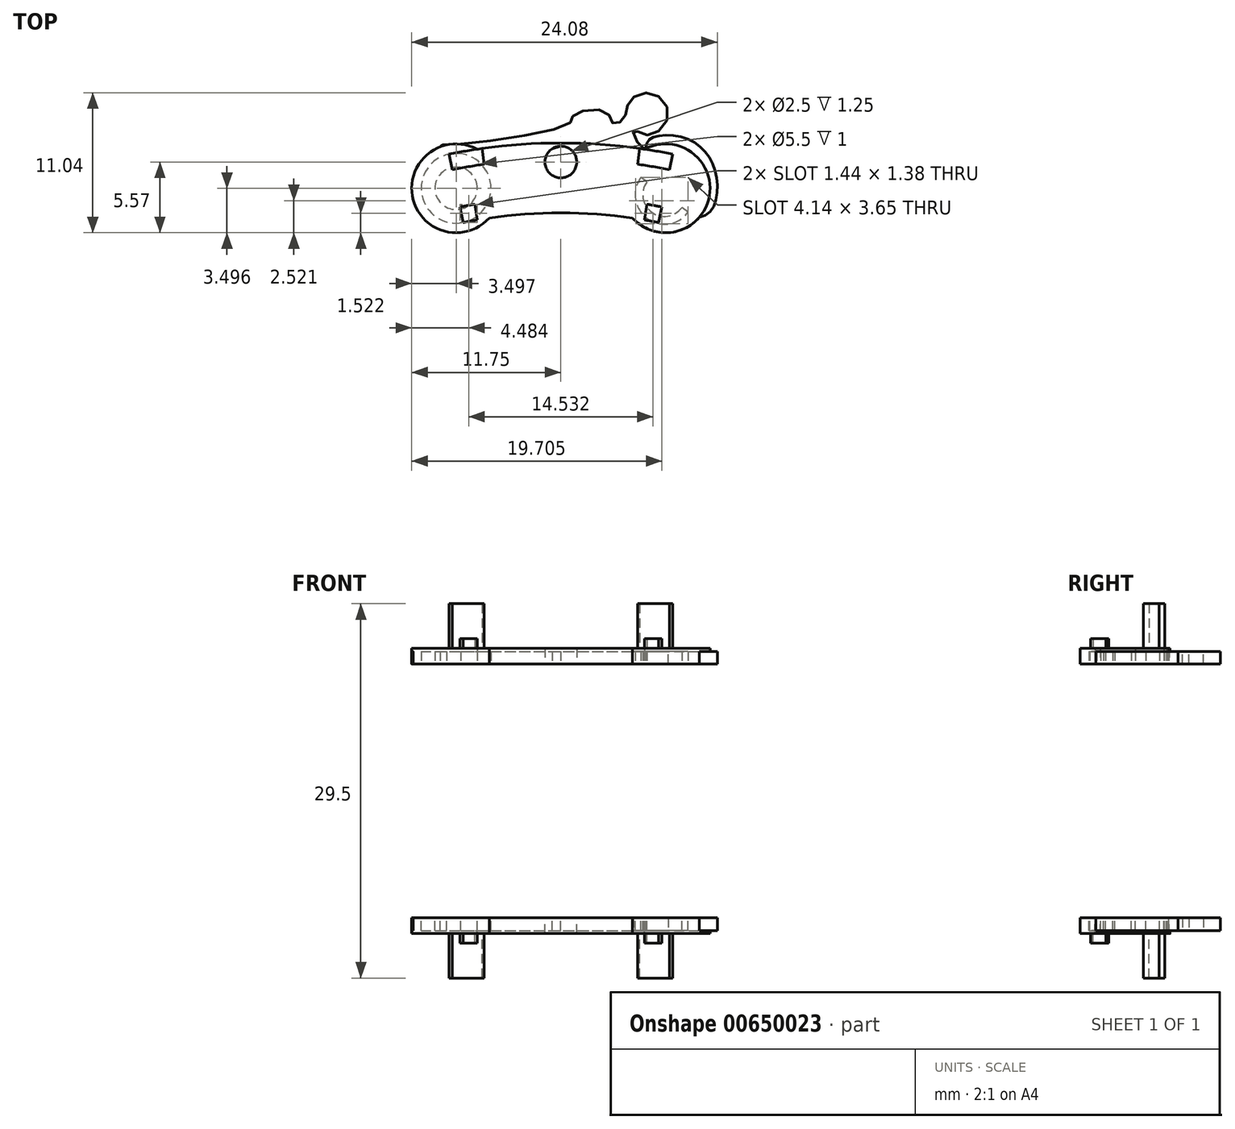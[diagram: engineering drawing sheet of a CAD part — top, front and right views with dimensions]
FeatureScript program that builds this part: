
annotation { "Feature Type Name" : "Feature", "Feature Type Description" : "" }
export const myFeature = defineFeature(function(context is Context, id is Id, definition is map)
    precondition{}
    {
        {
            var Q0;
            Q0=qCreatedBy(makeId("Top.planeOp"),FACE);
            var sketch = newSketch(context, id + "F0", { "sketchPlane" : qUnion([Q0])});
            skCircle(sketch, "E0", {"center": v(0, 0) * mm, "radius": 39 * mm});
            skCircle(sketch, "E1", {"center": v(0, 0) * mm, "radius": 44.5 * mm});
            skCircle(sketch, "E2", {"center": v(0, 43) * mm, "radius": 1.25 * mm});
            skCircle(sketch, "E3", {"center": v(0, 43) * mm, "radius": 6 * mm});
            skLineSegment(sketch, "E4", {"start": v(-7.7, 38.23) * mm, "end": v(-8.8, 43.62) * mm});
            skLineSegment(sketch, "E5", {"start": v(7.7, 38.23) * mm, "end": v(8.8, 43.62) * mm});
            skLineSegment(sketch, "E6", {"start": v(-7.5, 43.86) * mm, "end": v(-6.58, 38.44) * mm});
            skLineSegment(sketch, "E7", {"start": v(6.58, 38.44) * mm, "end": v(7.5, 43.86) * mm});
            skCircle(sketch, "E8", {"center": v(0, 0) * mm, "radius": 40.25 * mm});
            skCircle(sketch, "E9", {"center": v(0, 0) * mm, "radius": 43.25 * mm});
            skSolve(sketch);
        }
        {
            var Q0;
            {var subQ0=sQuery(id+"F0.wireOp",EDGE,"E7");var subQ1=sQuery(id+"F0.wireOp",EDGE,"E1");var subQ2=makeQuery(id+"F0.imprint","INTERSECT",VERTEX,{"derivedFrom":[subQ1,subQ0]});Q0=makeQuery(id+"F0.imprint","IMPRINT",FACE,{"disambiguationData":[TD([[makeQuery(id+"F0.imprint","IMPRINT",EDGE,{"disambiguationData":[TD([[subQ2,-1.0]])],"derivedFrom":subQ1}),1.0]])]});}
            var Q1;
            {var subQ0=sQuery(id+"F0.wireOp",EDGE,"E6");var subQ1=sQuery(id+"F0.wireOp",EDGE,"E1");var subQ2=makeQuery(id+"F0.imprint","INTERSECT",VERTEX,{"derivedFrom":[subQ1,subQ0]});Q1=makeQuery(id+"F0.imprint","IMPRINT",FACE,{"disambiguationData":[TD([[makeQuery(id+"F0.imprint","IMPRINT",EDGE,{"disambiguationData":[TD([[subQ2,1.0]])],"derivedFrom":subQ1}),1.0]])]});}
            var Q2;
            {var subQ0=sQuery(id+"F0.wireOp",EDGE,"E3");var subQ1=sQuery(id+"F0.wireOp",EDGE,"E1");var subQ2=makeQuery(id+"F0.imprint","INTERSECT",VERTEX,{"disambiguationData":[OD(0.0)],"derivedFrom":[subQ1,subQ0]});Q2=makeQuery(id+"F0.imprint","IMPRINT",FACE,{"disambiguationData":[TD([[makeQuery(id+"F0.imprint","IMPRINT",EDGE,{"disambiguationData":[TD([[subQ2,-1.0]])],"derivedFrom":subQ1}),1.0]])]});}
            var Q3;
            {var subQ0=sQuery(id+"F0.wireOp",EDGE,"E8");var subQ1=sQuery(id+"F0.wireOp",EDGE,"E3");var subQ2=makeQuery(id+"F0.imprint","INTERSECT",VERTEX,{"disambiguationData":[OD(1.0)],"derivedFrom":[subQ1,subQ0]});Q3=makeQuery(id+"F0.imprint","IMPRINT",FACE,{"disambiguationData":[TD([[makeQuery(id+"F0.imprint","IMPRINT",EDGE,{"disambiguationData":[TD([[subQ2,-1.0]])],"derivedFrom":subQ1}),-1.0]])]});}
            var Q4;
            {var subQ3=sQuery(id+"F0.wireOp",EDGE,"E9");var subQ5=sQuery(id+"F0.wireOp",EDGE,"E2");var subQ6=makeQuery(id+"F0.imprint","INTERSECT",VERTEX,{"disambiguationData":[OD(0.0)],"derivedFrom":[subQ5,subQ3]});Q4=makeQuery(id+"F0.imprint","IMPRINT",FACE,{"disambiguationData":[TD([[makeQuery(id+"F0.imprint","IMPRINT",EDGE,{"disambiguationData":[TD([[subQ6,1.0]])],"derivedFrom":subQ5}),-1.0]])]});}
            var Q5;
            {var subQ0=sQuery(id+"F0.wireOp",EDGE,"E9");var subQ1=sQuery(id+"F0.wireOp",EDGE,"E3");var subQ2=makeQuery(id+"F0.imprint","INTERSECT",VERTEX,{"disambiguationData":[OD(0.0)],"derivedFrom":[subQ1,subQ0]});Q5=makeQuery(id+"F0.imprint","IMPRINT",FACE,{"disambiguationData":[TD([[makeQuery(id+"F0.imprint","IMPRINT",EDGE,{"disambiguationData":[TD([[subQ2,-1.0]])],"derivedFrom":subQ1}),-1.0]])]});}
            var Q6;
            {var subQ0=sQuery(id+"F0.wireOp",EDGE,"E6");var subQ1=sQuery(id+"F0.wireOp",EDGE,"E0");var subQ2=makeQuery(id+"F0.imprint","INTERSECT",VERTEX,{"derivedFrom":[subQ1,subQ0]});Q6=makeQuery(id+"F0.imprint","IMPRINT",FACE,{"disambiguationData":[TD([[makeQuery(id+"F0.imprint","IMPRINT",EDGE,{"disambiguationData":[TD([[subQ2,1.0]])],"derivedFrom":subQ1}),-1.0]])]});}
            var Q7;
            {var subQ0=sQuery(id+"F0.wireOp",EDGE,"E3");var subQ1=sQuery(id+"F0.wireOp",EDGE,"E0");var subQ2=makeQuery(id+"F0.imprint","INTERSECT",VERTEX,{"disambiguationData":[OD(0.0)],"derivedFrom":[subQ1,subQ0]});Q7=makeQuery(id+"F0.imprint","IMPRINT",FACE,{"disambiguationData":[TD([[makeQuery(id+"F0.imprint","IMPRINT",EDGE,{"disambiguationData":[TD([[subQ2,-1.0]])],"derivedFrom":subQ1}),-1.0]])]});}
            var Q8;
            {var subQ0=sQuery(id+"F0.wireOp",EDGE,"E7");var subQ1=sQuery(id+"F0.wireOp",EDGE,"E0");var subQ2=makeQuery(id+"F0.imprint","INTERSECT",VERTEX,{"derivedFrom":[subQ1,subQ0]});Q8=makeQuery(id+"F0.imprint","IMPRINT",FACE,{"disambiguationData":[TD([[makeQuery(id+"F0.imprint","IMPRINT",EDGE,{"disambiguationData":[TD([[subQ2,-1.0]])],"derivedFrom":subQ1}),-1.0]])]});}
            var Q9;
            {var subQ0=sQuery(id+"F0.wireOp",EDGE,"E8");var subQ1=sQuery(id+"F0.wireOp",EDGE,"E5");var subQ2=makeQuery(id+"F0.imprint","INTERSECT",VERTEX,{"derivedFrom":[subQ1,subQ0]});Q9=makeQuery(id+"F0.imprint","IMPRINT",FACE,{"disambiguationData":[TD([[makeQuery(id+"F0.imprint","IMPRINT",EDGE,{"disambiguationData":[TD([[subQ2,-1.0]])],"derivedFrom":subQ1}),1.0]])]});}
            var Q10;
            {var subQ0=sQuery(id+"F0.wireOp",EDGE,"E8");var subQ1=sQuery(id+"F0.wireOp",EDGE,"E4");var subQ2=makeQuery(id+"F0.imprint","INTERSECT",VERTEX,{"derivedFrom":[subQ1,subQ0]});Q10=makeQuery(id+"F0.imprint","IMPRINT",FACE,{"disambiguationData":[TD([[makeQuery(id+"F0.imprint","IMPRINT",EDGE,{"disambiguationData":[TD([[subQ2,-1.0]])],"derivedFrom":subQ1}),-1.0]])]});}
            extrude(context, id + "F1", {"entities" : qUnion([Q0, Q1, Q2, Q3, Q4, Q5, Q6, Q7, Q8, Q9, Q10]), "depth" : 1.25 * mm, "offsetDistance" : 25 * mm});
        }
        {
            var Q0;
            Q0=qCreatedBy(makeId("Top.planeOp"),FACE);
            var sketch = newSketch(context, id + "F2", { "sketchPlane" : qUnion([Q0])});
            skCircle(sketch, "E10", {"center": v(0, 0) * mm, "radius": 39 * mm});
            skCircle(sketch, "E11", {"center": v(0, 0) * mm, "radius": 44.5 * mm});
            skCircle(sketch, "E12", {"center": v(0, 43) * mm, "radius": 0.85 * mm});
            skCircle(sketch, "E13", {"center": v(0, 43) * mm, "radius": 6 * mm});
            skLineSegment(sketch, "E14", {"start": v(-7.7, 38.23) * mm, "end": v(-8.8, 43.62) * mm});
            skLineSegment(sketch, "E15", {"start": v(7.7, 38.23) * mm, "end": v(8.8, 43.62) * mm});
            skLineSegment(sketch, "E16", {"start": v(-6.2, 44.06) * mm, "end": v(-5.44, 38.62) * mm});
            skLineSegment(sketch, "E17", {"start": v(5.44, 38.62) * mm, "end": v(6.2, 44.06) * mm});
            skCircle(sketch, "E18", {"center": v(0, 0) * mm, "radius": 40.25 * mm});
            skCircle(sketch, "E19", {"center": v(0, 0) * mm, "radius": 43.25 * mm});
            skSolve(sketch);
        }
        {
            var Q0;
            {var subQ0=sQuery(id+"F2.wireOp",EDGE,"E15");var subQ1=sQuery(id+"F2.wireOp",EDGE,"E11");var subQ2=makeQuery(id+"F2.imprint","INTERSECT",VERTEX,{"derivedFrom":[subQ1,subQ0]});Q0=makeQuery(id+"F2.imprint","IMPRINT",FACE,{"disambiguationData":[TD([[makeQuery(id+"F2.imprint","IMPRINT",EDGE,{"disambiguationData":[TD([[subQ2,-1.0]])],"derivedFrom":subQ1}),1.0]])]});}
            var Q1;
            {var subQ0=sQuery(id+"F2.wireOp",EDGE,"E14");var subQ1=sQuery(id+"F2.wireOp",EDGE,"E11");var subQ2=makeQuery(id+"F2.imprint","INTERSECT",VERTEX,{"derivedFrom":[subQ1,subQ0]});Q1=makeQuery(id+"F2.imprint","IMPRINT",FACE,{"disambiguationData":[TD([[makeQuery(id+"F2.imprint","IMPRINT",EDGE,{"disambiguationData":[TD([[subQ2,1.0]])],"derivedFrom":subQ1}),1.0]])]});}
            extrude(context, id + "F3", {"entities" : qUnion([Q0, Q1]), "operationType" : NewBodyOperationType.ADD, "depth" : 4.75 * mm, "offsetDistance" : 25 * mm});
        }
        {
            var Q0;
            Q0=qCreatedBy(makeId("Top.planeOp"),FACE);
            var sketch = newSketch(context, id + "F4", { "sketchPlane" : qUnion([Q0])});
            skCircle(sketch, "E20", {"center": v(0, 0) * mm, "radius": 39 * mm});
            skCircle(sketch, "E21", {"center": v(0, 0) * mm, "radius": 44.5 * mm});
            skCircle(sketch, "E22", {"center": v(0, 43) * mm, "radius": 0.85 * mm});
            skCircle(sketch, "E23", {"center": v(0, 43) * mm, "radius": 6 * mm});
            skLineSegment(sketch, "E24", {"start": v(-7.7, 38.23) * mm, "end": v(-8.8, 43.62) * mm});
            skLineSegment(sketch, "E25", {"start": v(7.7, 38.23) * mm, "end": v(8.8, 43.62) * mm});
            skLineSegment(sketch, "E26", {"start": v(-7.5, 43.86) * mm, "end": v(-6.58, 38.44) * mm});
            skLineSegment(sketch, "E27", {"start": v(6.58, 38.44) * mm, "end": v(7.5, 43.86) * mm});
            skCircle(sketch, "E28", {"center": v(0, 0) * mm, "radius": 40.25 * mm});
            skCircle(sketch, "E29", {"center": v(0, 0) * mm, "radius": 43.25 * mm});
            skSolve(sketch);
        }
        {
            var Q0;
            {var subQ0=sQuery(id+"F4.wireOp",EDGE,"E24");var subQ1=sQuery(id+"F4.wireOp",EDGE,"E20");var subQ2=makeQuery(id+"F4.imprint","INTERSECT",VERTEX,{"derivedFrom":[subQ1,subQ0]});Q0=makeQuery(id+"F4.imprint","IMPRINT",FACE,{"disambiguationData":[TD([[makeQuery(id+"F4.imprint","IMPRINT",EDGE,{"disambiguationData":[TD([[subQ2,1.0]])],"derivedFrom":subQ1}),-1.0]])]});}
            var Q1;
            {var subQ0=sQuery(id+"F4.wireOp",EDGE,"E25");var subQ1=sQuery(id+"F4.wireOp",EDGE,"E20");var subQ2=makeQuery(id+"F4.imprint","INTERSECT",VERTEX,{"derivedFrom":[subQ1,subQ0]});Q1=makeQuery(id+"F4.imprint","IMPRINT",FACE,{"disambiguationData":[TD([[makeQuery(id+"F4.imprint","IMPRINT",EDGE,{"disambiguationData":[TD([[subQ2,-1.0]])],"derivedFrom":subQ1}),-1.0]])]});}
            extrude(context, id + "F5", {"entities" : qUnion([Q0, Q1]), "operationType" : NewBodyOperationType.ADD, "depth" : 2 * mm, "offsetDistance" : 25 * mm});
        }
        {
            var Q0;
            {var subQ0=sQuery(id+"F4.wireOp",EDGE,"E28");var subQ1=sQuery(id+"F4.wireOp",EDGE,"E20");var subQ2=sQuery(id+"F2.wireOp",EDGE,"E19");var subQ3=sQuery(id+"F2.wireOp",EDGE,"E11");Q0=makeQuery(id+"F5.boolean.opBoolean","MERGE",FACE,{"derivedFrom":[makeQuery(id+"F3.boolean.opBoolean","MERGE",FACE,{"derivedFrom":[makeQuery(id+"F1.opExtrude","CAP_FACE",FACE,{"disambiguationData":[OSD([sQuery(id+"F0.wireOp",EDGE,"E0"),sQuery(id+"F0.wireOp",EDGE,"E1"),sQuery(id+"F0.wireOp",EDGE,"E2"),sQuery(id+"F0.wireOp",EDGE,"E4"),sQuery(id+"F0.wireOp",EDGE,"E5"),sQuery(id+"F0.wireOp",EDGE,"E6"),sQuery(id+"F0.wireOp",EDGE,"E7"),sQuery(id+"F0.wireOp",EDGE,"E8"),sQuery(id+"F0.wireOp",EDGE,"E9")])],"isStart":true}),makeQuery(id+"F3.opExtrude","CAP_FACE",FACE,{"disambiguationData":[OSD([subQ3,sQuery(id+"F2.wireOp",EDGE,"E15"),sQuery(id+"F2.wireOp",EDGE,"E17"),subQ2])],"isStart":true}),makeQuery(id+"F3.opExtrude","CAP_FACE",FACE,{"disambiguationData":[OSD([subQ3,sQuery(id+"F2.wireOp",EDGE,"E14"),sQuery(id+"F2.wireOp",EDGE,"E16"),subQ2])],"isStart":true})]}),makeQuery(id+"F5.opExtrude","CAP_FACE",FACE,{"disambiguationData":[OSD([subQ1,sQuery(id+"F4.wireOp",EDGE,"E25"),sQuery(id+"F4.wireOp",EDGE,"E27"),subQ0])],"isStart":true}),makeQuery(id+"F5.opExtrude","CAP_FACE",FACE,{"disambiguationData":[OSD([subQ1,sQuery(id+"F4.wireOp",EDGE,"E24"),sQuery(id+"F4.wireOp",EDGE,"E26"),subQ0])],"isStart":true})]});}
            var sketch = newSketch(context, id + "F6", { "sketchPlane" : qUnion([Q0])});
            skCircle(sketch, "E30", {"center": v(-8.25, -40.93) * mm, "radius": 3.5 * mm});
            skCircle(sketch, "E31", {"center": v(8.25, -40.93) * mm, "radius": 3.5 * mm});
            skSolve(sketch);
        }
        {
            var Q0;
            Q0 = qSketchRegion(id + "F6", true);
            extrude(context, id + "F7", {"entities" : qUnion([Q0]), "operationType" : NewBodyOperationType.ADD, "oppositeDirection" : true, "depth" : 1.25 * mm, "offsetDistance" : 25 * mm});
        }
        {
            var Q0;
            {var subQ0=sQuery(id+"F4.wireOp",EDGE,"E28");var subQ1=sQuery(id+"F4.wireOp",EDGE,"E20");var subQ2=sQuery(id+"F2.wireOp",EDGE,"E19");var subQ3=sQuery(id+"F2.wireOp",EDGE,"E11");Q0=makeQuery(id+"F7.boolean.opBoolean","MERGE",FACE,{"derivedFrom":[makeQuery(id+"F5.boolean.opBoolean","MERGE",FACE,{"derivedFrom":[makeQuery(id+"F3.boolean.opBoolean","MERGE",FACE,{"derivedFrom":[makeQuery(id+"F1.opExtrude","CAP_FACE",FACE,{"disambiguationData":[OSD([sQuery(id+"F0.wireOp",EDGE,"E0"),sQuery(id+"F0.wireOp",EDGE,"E1"),sQuery(id+"F0.wireOp",EDGE,"E2"),sQuery(id+"F0.wireOp",EDGE,"E4"),sQuery(id+"F0.wireOp",EDGE,"E5"),sQuery(id+"F0.wireOp",EDGE,"E6"),sQuery(id+"F0.wireOp",EDGE,"E7"),sQuery(id+"F0.wireOp",EDGE,"E8"),sQuery(id+"F0.wireOp",EDGE,"E9")])],"isStart":true}),makeQuery(id+"F3.opExtrude","CAP_FACE",FACE,{"disambiguationData":[OSD([subQ3,sQuery(id+"F2.wireOp",EDGE,"E15"),sQuery(id+"F2.wireOp",EDGE,"E17"),subQ2])],"isStart":true}),makeQuery(id+"F3.opExtrude","CAP_FACE",FACE,{"disambiguationData":[OSD([subQ3,sQuery(id+"F2.wireOp",EDGE,"E14"),sQuery(id+"F2.wireOp",EDGE,"E16"),subQ2])],"isStart":true})]}),makeQuery(id+"F5.opExtrude","CAP_FACE",FACE,{"disambiguationData":[OSD([subQ1,sQuery(id+"F4.wireOp",EDGE,"E25"),sQuery(id+"F4.wireOp",EDGE,"E27"),subQ0])],"isStart":true}),makeQuery(id+"F5.opExtrude","CAP_FACE",FACE,{"disambiguationData":[OSD([subQ1,sQuery(id+"F4.wireOp",EDGE,"E24"),sQuery(id+"F4.wireOp",EDGE,"E26"),subQ0])],"isStart":true})]}),makeQuery(id+"F7.opExtrude","CAP_FACE",FACE,{"disambiguationData":[OSD([sQuery(id+"F6.wireOp",EDGE,"E30")])],"isStart":true}),makeQuery(id+"F7.opExtrude","CAP_FACE",FACE,{"disambiguationData":[OSD([sQuery(id+"F6.wireOp",EDGE,"E31")])],"isStart":true})]});}
            var sketch = newSketch(context, id + "F8", { "sketchPlane" : qUnion([Q0])});
            skPoint(sketch, "E32.19.internal.snap0", {"position": v(0, -39) * mm});
            skFitSpline(sketch, "E32", {"points": [v(-9.52, -44.2) * mm, v(-9.01, -44.34) * mm, v(0.7, -46.06) * mm, v(1, -46.68) * mm, v(3.57, -46.95) * mm, v(4.12, -46.04) * mm, v(4.97, -46.43) * mm, v(5.33, -47.68) * mm, v(7.05, -48.44) * mm, v(8.48, -46.78) * mm, v(7.01, -45.12) * mm, v(5.85, -45.47) * mm, v(5.7, -45.23) * mm, v(6.6, -44) * mm, v(6.86, -44.64) * mm, v(10.09, -44.77) * mm, v(12.3, -41.5) * mm, v(10.9, -38.63) * mm, v(2.21, -43.47) * mm, v(0, -44.25) * mm, v(-9.77, -40.16) * mm, v(-10.2, -40.1) * mm, v(-11.62, -39.98) * mm, v(-9.52, -44.2) * mm]});
            skSolve(sketch);
        }
        {
            var Q0;
            Q0 = qSketchRegion(id + "F8", true);
            extrude(context, id + "F9", {"entities" : qUnion([Q0]), "operationType" : NewBodyOperationType.ADD, "oppositeDirection" : true, "depth" : 1 * mm, "offsetDistance" : 25 * mm});
        }
        {
            var Q0;
            {var subQ0=sQuery(id+"F4.wireOp",EDGE,"E28");var subQ1=sQuery(id+"F4.wireOp",EDGE,"E20");var subQ2=sQuery(id+"F2.wireOp",EDGE,"E19");var subQ3=sQuery(id+"F2.wireOp",EDGE,"E11");Q0=makeQuery(id+"F9.boolean.opBoolean","MERGE",FACE,{"derivedFrom":[makeQuery(id+"F7.boolean.opBoolean","MERGE",FACE,{"derivedFrom":[makeQuery(id+"F5.boolean.opBoolean","MERGE",FACE,{"derivedFrom":[makeQuery(id+"F3.boolean.opBoolean","MERGE",FACE,{"derivedFrom":[makeQuery(id+"F1.opExtrude","CAP_FACE",FACE,{"disambiguationData":[OSD([sQuery(id+"F0.wireOp",EDGE,"E0"),sQuery(id+"F0.wireOp",EDGE,"E1"),sQuery(id+"F0.wireOp",EDGE,"E2"),sQuery(id+"F0.wireOp",EDGE,"E4"),sQuery(id+"F0.wireOp",EDGE,"E5"),sQuery(id+"F0.wireOp",EDGE,"E6"),sQuery(id+"F0.wireOp",EDGE,"E7"),sQuery(id+"F0.wireOp",EDGE,"E8"),sQuery(id+"F0.wireOp",EDGE,"E9")])],"isStart":true}),makeQuery(id+"F3.opExtrude","CAP_FACE",FACE,{"disambiguationData":[OSD([subQ3,sQuery(id+"F2.wireOp",EDGE,"E15"),sQuery(id+"F2.wireOp",EDGE,"E17"),subQ2])],"isStart":true}),makeQuery(id+"F3.opExtrude","CAP_FACE",FACE,{"disambiguationData":[OSD([subQ3,sQuery(id+"F2.wireOp",EDGE,"E14"),sQuery(id+"F2.wireOp",EDGE,"E16"),subQ2])],"isStart":true})]}),makeQuery(id+"F5.opExtrude","CAP_FACE",FACE,{"disambiguationData":[OSD([subQ1,sQuery(id+"F4.wireOp",EDGE,"E25"),sQuery(id+"F4.wireOp",EDGE,"E27"),subQ0])],"isStart":true}),makeQuery(id+"F5.opExtrude","CAP_FACE",FACE,{"disambiguationData":[OSD([subQ1,sQuery(id+"F4.wireOp",EDGE,"E24"),sQuery(id+"F4.wireOp",EDGE,"E26"),subQ0])],"isStart":true})]}),makeQuery(id+"F7.opExtrude","CAP_FACE",FACE,{"disambiguationData":[OSD([sQuery(id+"F6.wireOp",EDGE,"E30")])],"isStart":true}),makeQuery(id+"F7.opExtrude","CAP_FACE",FACE,{"disambiguationData":[OSD([sQuery(id+"F6.wireOp",EDGE,"E31")])],"isStart":true})]}),makeQuery(id+"F9.opExtrude","CAP_FACE",FACE,{"disambiguationData":[OSD([sQuery(id+"F8.wireOp",EDGE,"E32")])],"isStart":true})]});}
            var sketch = newSketch(context, id + "F10", { "sketchPlane" : qUnion([Q0])});
            skCircle(sketch, "E33", {"center": v(-8.25, -40.93) * mm, "radius": 2.75 * mm});
            skSolve(sketch);
        }
        {
            var Q0;
            Q0=makeQuery(id+"F10.imprint","IMPRINT",FACE,{"disambiguationData":[TD([[makeQuery(id+"F10.imprint","IMPRINT",EDGE,{"derivedFrom":sQuery(id+"F10.wireOp",EDGE,"E33")}),1.0]])]});
            var Q1;
            Q1=sQuery(id+"F10.wireOp",EDGE,"E33");
            extrude(context, id + "F11", {"entities" : qUnion([Q0]), "operationType" : NewBodyOperationType.REMOVE, "surfaceEntities" : qUnion([Q1]), "oppositeDirection" : true, "depth" : 1 * mm, "offsetDistance" : 25 * mm});
        }
        {
            var Q0;
            {var subQ0=sQuery(id+"F4.wireOp",EDGE,"E28");var subQ1=sQuery(id+"F4.wireOp",EDGE,"E20");var subQ2=sQuery(id+"F2.wireOp",EDGE,"E19");var subQ3=sQuery(id+"F2.wireOp",EDGE,"E11");Q0=makeQuery(id+"F9.boolean.opBoolean","MERGE",FACE,{"derivedFrom":[makeQuery(id+"F7.boolean.opBoolean","MERGE",FACE,{"derivedFrom":[makeQuery(id+"F5.boolean.opBoolean","MERGE",FACE,{"derivedFrom":[makeQuery(id+"F3.boolean.opBoolean","MERGE",FACE,{"derivedFrom":[makeQuery(id+"F1.opExtrude","CAP_FACE",FACE,{"disambiguationData":[OSD([sQuery(id+"F0.wireOp",EDGE,"E0"),sQuery(id+"F0.wireOp",EDGE,"E1"),sQuery(id+"F0.wireOp",EDGE,"E2"),sQuery(id+"F0.wireOp",EDGE,"E4"),sQuery(id+"F0.wireOp",EDGE,"E5"),sQuery(id+"F0.wireOp",EDGE,"E6"),sQuery(id+"F0.wireOp",EDGE,"E7"),sQuery(id+"F0.wireOp",EDGE,"E8"),sQuery(id+"F0.wireOp",EDGE,"E9")])],"isStart":true}),makeQuery(id+"F3.opExtrude","CAP_FACE",FACE,{"disambiguationData":[OSD([subQ3,sQuery(id+"F2.wireOp",EDGE,"E15"),sQuery(id+"F2.wireOp",EDGE,"E17"),subQ2])],"isStart":true}),makeQuery(id+"F3.opExtrude","CAP_FACE",FACE,{"disambiguationData":[OSD([subQ3,sQuery(id+"F2.wireOp",EDGE,"E14"),sQuery(id+"F2.wireOp",EDGE,"E16"),subQ2])],"isStart":true})]}),makeQuery(id+"F5.opExtrude","CAP_FACE",FACE,{"disambiguationData":[OSD([subQ1,sQuery(id+"F4.wireOp",EDGE,"E25"),sQuery(id+"F4.wireOp",EDGE,"E27"),subQ0])],"isStart":true}),makeQuery(id+"F5.opExtrude","CAP_FACE",FACE,{"disambiguationData":[OSD([subQ1,sQuery(id+"F4.wireOp",EDGE,"E24"),sQuery(id+"F4.wireOp",EDGE,"E26"),subQ0])],"isStart":true})]}),makeQuery(id+"F7.opExtrude","CAP_FACE",FACE,{"disambiguationData":[OSD([sQuery(id+"F6.wireOp",EDGE,"E30")])],"isStart":true}),makeQuery(id+"F7.opExtrude","CAP_FACE",FACE,{"disambiguationData":[OSD([sQuery(id+"F6.wireOp",EDGE,"E31")])],"isStart":true})]}),makeQuery(id+"F9.opExtrude","CAP_FACE",FACE,{"disambiguationData":[OSD([sQuery(id+"F8.wireOp",EDGE,"E32")])],"isStart":true})]});}
            var sketch = newSketch(context, id + "F12", { "sketchPlane" : qUnion([Q0])});
            skCircle(sketch, "E34", {"center": v(-8.25, -40.93) * mm, "radius": 1.67 * mm});
            skSolve(sketch);
        }
        {
            var Q0;
            Q0 = qSketchRegion(id + "F12", true);
            extrude(context, id + "F13", {"entities" : qUnion([Q0]), "operationType" : NewBodyOperationType.ADD, "oppositeDirection" : true, "depth" : 1 * mm, "offsetDistance" : 25 * mm});
        }
        {
            var Q0;
            {var subQ0=sQuery(id+"F4.wireOp",EDGE,"E28");var subQ1=sQuery(id+"F4.wireOp",EDGE,"E20");var subQ2=sQuery(id+"F2.wireOp",EDGE,"E19");var subQ3=sQuery(id+"F2.wireOp",EDGE,"E11");Q0=makeQuery(id+"F9.boolean.opBoolean","MERGE",FACE,{"derivedFrom":[makeQuery(id+"F7.boolean.opBoolean","MERGE",FACE,{"derivedFrom":[makeQuery(id+"F5.boolean.opBoolean","MERGE",FACE,{"derivedFrom":[makeQuery(id+"F3.boolean.opBoolean","MERGE",FACE,{"derivedFrom":[makeQuery(id+"F1.opExtrude","CAP_FACE",FACE,{"disambiguationData":[OSD([sQuery(id+"F0.wireOp",EDGE,"E0"),sQuery(id+"F0.wireOp",EDGE,"E1"),sQuery(id+"F0.wireOp",EDGE,"E2"),sQuery(id+"F0.wireOp",EDGE,"E4"),sQuery(id+"F0.wireOp",EDGE,"E5"),sQuery(id+"F0.wireOp",EDGE,"E6"),sQuery(id+"F0.wireOp",EDGE,"E7"),sQuery(id+"F0.wireOp",EDGE,"E8"),sQuery(id+"F0.wireOp",EDGE,"E9")])],"isStart":true}),makeQuery(id+"F3.opExtrude","CAP_FACE",FACE,{"disambiguationData":[OSD([subQ3,sQuery(id+"F2.wireOp",EDGE,"E15"),sQuery(id+"F2.wireOp",EDGE,"E17"),subQ2])],"isStart":true}),makeQuery(id+"F3.opExtrude","CAP_FACE",FACE,{"disambiguationData":[OSD([subQ3,sQuery(id+"F2.wireOp",EDGE,"E14"),sQuery(id+"F2.wireOp",EDGE,"E16"),subQ2])],"isStart":true})]}),makeQuery(id+"F5.opExtrude","CAP_FACE",FACE,{"disambiguationData":[OSD([subQ1,sQuery(id+"F4.wireOp",EDGE,"E25"),sQuery(id+"F4.wireOp",EDGE,"E27"),subQ0])],"isStart":true}),makeQuery(id+"F5.opExtrude","CAP_FACE",FACE,{"disambiguationData":[OSD([subQ1,sQuery(id+"F4.wireOp",EDGE,"E24"),sQuery(id+"F4.wireOp",EDGE,"E26"),subQ0])],"isStart":true})]}),makeQuery(id+"F7.opExtrude","CAP_FACE",FACE,{"disambiguationData":[OSD([sQuery(id+"F6.wireOp",EDGE,"E30")])],"isStart":true}),makeQuery(id+"F7.opExtrude","CAP_FACE",FACE,{"disambiguationData":[OSD([sQuery(id+"F6.wireOp",EDGE,"E31")])],"isStart":true})]}),makeQuery(id+"F9.opExtrude","CAP_FACE",FACE,{"disambiguationData":[OSD([sQuery(id+"F8.wireOp",EDGE,"E32")])],"isStart":true})]});}
            var sketch = newSketch(context, id + "F14", { "sketchPlane" : qUnion([Q0])});
            skArc(sketch, "E35", {"start": v(10.02, -39.04) * mm, "mid": v(6.8, -38.55) * mm, "end": v(6.3, -41.77) * mm});
            skLineSegment(sketch, "E36", {"start": v(10.02, -39.04) * mm, "end": v(6.3, -41.77) * mm});
            skSolve(sketch);
        }
        {
            var Q0;
            Q0 = qSketchRegion(id + "F14", true);
            extrude(context, id + "F15", {"entities" : qUnion([Q0]), "operationType" : NewBodyOperationType.REMOVE, "oppositeDirection" : true, "depth" : 1 * mm, "offsetDistance" : 25 * mm});
        }
        {
            var Q0;
            {var subQ0=sQuery(id+"F4.wireOp",EDGE,"E28");var subQ1=sQuery(id+"F4.wireOp",EDGE,"E20");var subQ2=sQuery(id+"F2.wireOp",EDGE,"E19");var subQ3=sQuery(id+"F2.wireOp",EDGE,"E11");Q0=makeQuery(id+"F9.boolean.opBoolean","MERGE",FACE,{"derivedFrom":[makeQuery(id+"F7.boolean.opBoolean","MERGE",FACE,{"derivedFrom":[makeQuery(id+"F5.boolean.opBoolean","MERGE",FACE,{"derivedFrom":[makeQuery(id+"F3.boolean.opBoolean","MERGE",FACE,{"derivedFrom":[makeQuery(id+"F1.opExtrude","CAP_FACE",FACE,{"disambiguationData":[OSD([sQuery(id+"F0.wireOp",EDGE,"E0"),sQuery(id+"F0.wireOp",EDGE,"E1"),sQuery(id+"F0.wireOp",EDGE,"E2"),sQuery(id+"F0.wireOp",EDGE,"E4"),sQuery(id+"F0.wireOp",EDGE,"E5"),sQuery(id+"F0.wireOp",EDGE,"E6"),sQuery(id+"F0.wireOp",EDGE,"E7"),sQuery(id+"F0.wireOp",EDGE,"E8"),sQuery(id+"F0.wireOp",EDGE,"E9")])],"isStart":true}),makeQuery(id+"F3.opExtrude","CAP_FACE",FACE,{"disambiguationData":[OSD([subQ3,sQuery(id+"F2.wireOp",EDGE,"E15"),sQuery(id+"F2.wireOp",EDGE,"E17"),subQ2])],"isStart":true}),makeQuery(id+"F3.opExtrude","CAP_FACE",FACE,{"disambiguationData":[OSD([subQ3,sQuery(id+"F2.wireOp",EDGE,"E14"),sQuery(id+"F2.wireOp",EDGE,"E16"),subQ2])],"isStart":true})]}),makeQuery(id+"F5.opExtrude","CAP_FACE",FACE,{"disambiguationData":[OSD([subQ1,sQuery(id+"F4.wireOp",EDGE,"E25"),sQuery(id+"F4.wireOp",EDGE,"E27"),subQ0])],"isStart":true}),makeQuery(id+"F5.opExtrude","CAP_FACE",FACE,{"disambiguationData":[OSD([subQ1,sQuery(id+"F4.wireOp",EDGE,"E24"),sQuery(id+"F4.wireOp",EDGE,"E26"),subQ0])],"isStart":true})]}),makeQuery(id+"F7.opExtrude","CAP_FACE",FACE,{"disambiguationData":[OSD([sQuery(id+"F6.wireOp",EDGE,"E30")])],"isStart":true}),makeQuery(id+"F7.opExtrude","CAP_FACE",FACE,{"disambiguationData":[OSD([sQuery(id+"F6.wireOp",EDGE,"E31")])],"isStart":true})]}),makeQuery(id+"F9.opExtrude","CAP_FACE",FACE,{"disambiguationData":[OSD([sQuery(id+"F8.wireOp",EDGE,"E32")])],"isStart":true})]});}
            var sketch = newSketch(context, id + "F16", { "sketchPlane" : qUnion([Q0])});
            skArc(sketch, "E37", {"start": v(9.55, -39.42) * mm, "mid": v(7.15, -39.05) * mm, "end": v(6.79, -41.44) * mm});
            skLineSegment(sketch, "E38", {"start": v(9.55, -39.42) * mm, "end": v(6.79, -41.44) * mm});
            skSolve(sketch);
        }
        {
            var Q0;
            Q0 = qSketchRegion(id + "F16", true);
            extrude(context, id + "F17", {"entities" : qUnion([Q0]), "operationType" : NewBodyOperationType.ADD, "oppositeDirection" : true, "depth" : 1 * mm, "offsetDistance" : 25 * mm});
        }
        {
            var Q0;
            Q0=makeQuery(id+"F1.opExtrude","SWEPT_BODY",BODY,{"disambiguationData":[OSD([sQuery(id+"F0.wireOp",EDGE,"E0"),sQuery(id+"F0.wireOp",EDGE,"E1"),sQuery(id+"F0.wireOp",EDGE,"E2"),sQuery(id+"F0.wireOp",EDGE,"E4"),sQuery(id+"F0.wireOp",EDGE,"E5"),sQuery(id+"F0.wireOp",EDGE,"E6"),sQuery(id+"F0.wireOp",EDGE,"E7"),sQuery(id+"F0.wireOp",EDGE,"E8"),sQuery(id+"F0.wireOp",EDGE,"E9")])]});
            transform(context, id + "F18", {"entities" : qUnion([Q0]), "transformType" : TransformType.TRANSLATION_3D, "dx" : 0 * mm, "dy" : 0 * mm, "dz" : 10 * mm, "makeCopy" : false});
        }
        {
            var Q0;
            Q0=makeQuery(id+"F1.opExtrude","SWEPT_BODY",BODY,{"disambiguationData":[OSD([sQuery(id+"F0.wireOp",EDGE,"E0"),sQuery(id+"F0.wireOp",EDGE,"E1"),sQuery(id+"F0.wireOp",EDGE,"E2"),sQuery(id+"F0.wireOp",EDGE,"E4"),sQuery(id+"F0.wireOp",EDGE,"E5"),sQuery(id+"F0.wireOp",EDGE,"E6"),sQuery(id+"F0.wireOp",EDGE,"E7"),sQuery(id+"F0.wireOp",EDGE,"E8"),sQuery(id+"F0.wireOp",EDGE,"E9")])]});
            var Q1;
            Q1=qCreatedBy(makeId("Top.planeOp"),FACE);
            mirror(context, id + "F19", {"entities" : qUnion([Q0]), "mirrorPlane" : qUnion([Q1])});
        }
    });
